# Revit family: Legrand XL³-S 160 flush-mounting
name_source: partatom
category: Equipement électrique
units: mm (PartAtom-declared; Revit-internal decimal feet)

## family parameters
Basée sur le plan de construction = Non
Configuration du panneau = Deux colonnes, circuits au sein
Cote de connecteur circulaire = Utiliser le diamètre
Couper avec des vides une fois chargée = Non
Numéro OmniClass = 23.80.30.11.17
Partagée = Non
Point de calcul de pièce = Non
Titre OmniClass = Distribution Boards and Control Panels
Toujours verticalement = Oui
Type d'élément = Tableau de raccordement

## types (12) — shared parameters
ETIM Class 6.0 = EC000261
Fabricant = Legrand
General Conditions of Use = https://export.legrand.com
IK = 07
IP = 40
Image du type = XL3S160_encastre_337224_p_231245.jpg
Material = Steel
RAL = 9003
URL = www.legrand.fr
depth = 138 mm  [stored 0.452756 ft]
depth Fluxh-mounting = 116 mm  [stored 0.380577 ft]
distance side installation zone = 138 mm  [stored 0.452756 ft]
door = Oui
weight = 0.00 kg
zero-valued in all types: Elévation par défaut

## per-type parameters (varying)
- Distribution envelope - XL³ S 160 Métal - flush-mounting - 24 modules - 2 rows: Cabinet 337222=Oui; Cabinet 337223=Non; Cabinet 337224=Non; Cabinet 337225=Non; Cabinet 337226=Non; Cabinet 337227=Non; Cabinet 337228=Non; Cabinet 337234=Non; Cabinet 337235=Non; Cabinet 337236=Non; Cabinet 337237=Non; Cabinet 337238=Non; Description=337222  Distribution envelope - XL³ S 160 Métal - flush-mounting - 24 modules - 2 rows; depth installation zone=805 mm  [stored 2.64108 ft]; distance before installation zone=667 mm  [stored 2.18832 ft]; door 337252=Oui; door 337253=Non; door 337254=Non; door 337255=Non; door 337256=Non; door 337257=Non; door 337258=Non; door 337264=Non; door 337265=Non; door 337266=Non; door 337267=Non; door 337268=Non; height 1=512 mm  [stored 1.67979 ft]; height 2=440 mm  [stored 1.44357 ft]; module (24 or 36)=24; number row=2; width=667 mm  [stored 2.18832 ft]; width installation zone=943 mm  [stored 3.09383 ft]
- Distribution envelope - XL³ S 160 Métal - flush-mounting - 24 modules - 3 rows: Cabinet 337222=Non; Cabinet 337223=Oui; Cabinet 337224=Non; Cabinet 337225=Non; Cabinet 337226=Non; Cabinet 337227=Non; Cabinet 337228=Non; Cabinet 337234=Non; Cabinet 337235=Non; Cabinet 337236=Non; Cabinet 337237=Non; Cabinet 337238=Non; Description=337223  Distribution envelope - XL³ S 160 Métal - flush-mounting - 24 modules - 3 rows; depth installation zone=805 mm  [stored 2.64108 ft]; distance before installation zone=667 mm  [stored 2.18832 ft]; door 337252=Non; door 337253=Oui; door 337254=Non; door 337255=Non; door 337256=Non; door 337257=Non; door 337258=Non; door 337264=Non; door 337265=Non; door 337266=Non; door 337267=Non; door 337268=Non; height 1=662 mm  [stored 2.17192 ft]; height 2=590 mm  [stored 1.9357 ft]; module (24 or 36)=24; number row=3; width=667 mm  [stored 2.18832 ft]; width installation zone=943 mm  [stored 3.09383 ft]
- Distribution envelope - XL³ S 160 Métal - flush-mounting - 24 modules - 4 rows: Cabinet 337222=Non; Cabinet 337223=Non; Cabinet 337224=Oui; Cabinet 337225=Non; Cabinet 337226=Non; Cabinet 337227=Non; Cabinet 337228=Non; Cabinet 337234=Non; Cabinet 337235=Non; Cabinet 337236=Non; Cabinet 337237=Non; Cabinet 337238=Non; Description=337224  Distribution envelope - XL³ S 160 Métal - flush-mounting - 24 modules - 4 rows; depth installation zone=805 mm  [stored 2.64108 ft]; distance before installation zone=667 mm  [stored 2.18832 ft]; door 337252=Non; door 337253=Non; door 337254=Oui; door 337255=Non; door 337256=Non; door 337257=Non; door 337258=Non; door 337264=Non; door 337265=Non; door 337266=Non; door 337267=Non; door 337268=Non; height 1=812 mm  [stored 2.66404 ft]; height 2=740 mm  [stored 2.42782 ft]; module (24 or 36)=24; number row=4; width=667 mm  [stored 2.18832 ft]; width installation zone=943 mm  [stored 3.09383 ft]
- Distribution envelope - XL³ S 160 Métal - flush-mounting - 24 modules - 5 rows: Cabinet 337222=Non; Cabinet 337223=Non; Cabinet 337224=Non; Cabinet 337225=Oui; Cabinet 337226=Non; Cabinet 337227=Non; Cabinet 337228=Non; Cabinet 337234=Non; Cabinet 337235=Non; Cabinet 337236=Non; Cabinet 337237=Non; Cabinet 337238=Non; Description=337225  Distribution envelope - XL³ S 160 Métal - flush-mounting - 24 modules - 5 rows; depth installation zone=805 mm  [stored 2.64108 ft]; distance before installation zone=667 mm  [stored 2.18832 ft]; door 337252=Non; door 337253=Non; door 337254=Non; door 337255=Oui; door 337256=Non; door 337257=Non; door 337258=Non; door 337264=Non; door 337265=Non; door 337266=Non; door 337267=Non; door 337268=Non; height 1=962 mm  [stored 3.15617 ft]; height 2=890 mm  [stored 2.91995 ft]; module (24 or 36)=24; number row=5; width=667 mm  [stored 2.18832 ft]; width installation zone=943 mm  [stored 3.09383 ft]
- Distribution envelope - XL³ S 160 Métal - flush-mounting - 24 modules - 6 rows: Cabinet 337222=Non; Cabinet 337223=Non; Cabinet 337224=Non; Cabinet 337225=Non; Cabinet 337226=Oui; Cabinet 337227=Non; Cabinet 337228=Non; Cabinet 337234=Non; Cabinet 337235=Non; Cabinet 337236=Non; Cabinet 337237=Non; Cabinet 337238=Non; Description=337226  Distribution envelope - XL³ S 160 Métal - flush-mounting - 24 modules - 6 rows; depth installation zone=805 mm  [stored 2.64108 ft]; distance before installation zone=667 mm  [stored 2.18832 ft]; door 337252=Non; door 337253=Non; door 337254=Non; door 337255=Non; door 337256=Oui; door 337257=Non; door 337258=Non; door 337264=Non; door 337265=Non; door 337266=Non; door 337267=Non; door 337268=Non; height 1=1112 mm  [stored 3.64829 ft]; height 2=1040 mm  [stored 3.41207 ft]; module (24 or 36)=24; number row=6; width=667 mm  [stored 2.18832 ft]; width installation zone=943 mm  [stored 3.09383 ft]
- Distribution envelope - XL³ S 160 Métal - flush-mounting - 24 modules - 7 rows: Cabinet 337222=Non; Cabinet 337223=Non; Cabinet 337224=Non; Cabinet 337225=Non; Cabinet 337226=Non; Cabinet 337227=Oui; Cabinet 337228=Non; Cabinet 337234=Non; Cabinet 337235=Non; Cabinet 337236=Non; Cabinet 337237=Non; Cabinet 337238=Non; Description=337227  Distribution envelope - XL³ S 160 Métal - flush-mounting - 24 modules - 7 rows; depth installation zone=805 mm  [stored 2.64108 ft]; distance before installation zone=667 mm  [stored 2.18832 ft]; door 337252=Non; door 337253=Non; door 337254=Non; door 337255=Non; door 337256=Non; door 337257=Oui; door 337258=Non; door 337264=Non; door 337265=Non; door 337266=Non; door 337267=Non; door 337268=Non; height 1=1262 mm  [stored 4.14042 ft]; height 2=1190 mm  [stored 3.9042 ft]; module (24 or 36)=24; number row=7; width=667 mm  [stored 2.18832 ft]; width installation zone=943 mm  [stored 3.09383 ft]
- Distribution envelope - XL³ S 160 Métal - flush-mounting - 24 modules - 8 rows: Cabinet 337222=Non; Cabinet 337223=Non; Cabinet 337224=Non; Cabinet 337225=Non; Cabinet 337226=Non; Cabinet 337227=Non; Cabinet 337228=Oui; Cabinet 337234=Non; Cabinet 337235=Non; Cabinet 337236=Non; Cabinet 337237=Non; Cabinet 337238=Non; Description=337228  Distribution envelope - XL³ S 160 Métal - flush-mounting - 24 modules - 8 rows; depth installation zone=805 mm  [stored 2.64108 ft]; distance before installation zone=667 mm  [stored 2.18832 ft]; door 337252=Non; door 337253=Non; door 337254=Non; door 337255=Non; door 337256=Non; door 337257=Non; door 337258=Oui; door 337264=Non; door 337265=Non; door 337266=Non; door 337267=Non; door 337268=Non; height 1=1412 mm  [stored 4.63255 ft]; height 2=1340 mm  [stored 4.39633 ft]; module (24 or 36)=24; number row=8; width=667 mm  [stored 2.18832 ft]; width installation zone=943 mm  [stored 3.09383 ft]
- Distribution envelope - XL³ S 160 Métal - flush-mounting - 36 modules - 4 rows: Cabinet 337222=Non; Cabinet 337223=Non; Cabinet 337224=Non; Cabinet 337225=Non; Cabinet 337226=Non; Cabinet 337227=Non; Cabinet 337228=Non; Cabinet 337234=Oui; Cabinet 337235=Non; Cabinet 337236=Non; Cabinet 337237=Non; Cabinet 337238=Non; Description=337234  Distribution envelope - XL³ S 160 Métal - flush-mounting - 36 modules - 4 rows; depth installation zone=1021 mm  [stored 3.34974 ft]; distance before installation zone=883 mm  [stored 2.89698 ft]; door 337252=Non; door 337253=Non; door 337254=Non; door 337255=Non; door 337256=Non; door 337257=Non; door 337258=Non; door 337264=Oui; door 337265=Non; door 337266=Non; door 337267=Non; door 337268=Non; height 1=812 mm  [stored 2.66404 ft]; height 2=740 mm  [stored 2.42782 ft]; module (24 or 36)=36; number row=4; width=883 mm  [stored 2.89698 ft]; width installation zone=1159 mm
- Distribution envelope - XL³ S 160 Métal - flush-mounting - 36 modules - 5 rows: Cabinet 337222=Non; Cabinet 337223=Non; Cabinet 337224=Non; Cabinet 337225=Non; Cabinet 337226=Non; Cabinet 337227=Non; Cabinet 337228=Non; Cabinet 337234=Non; Cabinet 337235=Oui; Cabinet 337236=Non; Cabinet 337237=Non; Cabinet 337238=Non; Description=337235  Distribution envelope - XL³ S 160 Métal - flush-mounting - 36 modules - 5 rows; depth installation zone=1021 mm  [stored 3.34974 ft]; distance before installation zone=883 mm  [stored 2.89698 ft]; door 337252=Non; door 337253=Non; door 337254=Non; door 337255=Non; door 337256=Non; door 337257=Non; door 337258=Non; door 337264=Non; door 337265=Oui; door 337266=Non; door 337267=Non; door 337268=Non; height 1=962 mm  [stored 3.15617 ft]; height 2=890 mm  [stored 2.91995 ft]; module (24 or 36)=36; number row=5; width=883 mm  [stored 2.89698 ft]; width installation zone=1159 mm
- Distribution envelope - XL³ S 160 Métal - flush-mounting - 36 modules - 6 rows: Cabinet 337222=Non; Cabinet 337223=Non; Cabinet 337224=Non; Cabinet 337225=Non; Cabinet 337226=Non; Cabinet 337227=Non; Cabinet 337228=Non; Cabinet 337234=Non; Cabinet 337235=Non; Cabinet 337236=Oui; Cabinet 337237=Non; Cabinet 337238=Non; Description=337236  Distribution envelope - XL³ S 160 Métal - flush-mounting - 36 modules - 6 rows; depth installation zone=1021 mm  [stored 3.34974 ft]; distance before installation zone=883 mm  [stored 2.89698 ft]; door 337252=Non; door 337253=Non; door 337254=Non; door 337255=Non; door 337256=Non; door 337257=Non; door 337258=Non; door 337264=Non; door 337265=Non; door 337266=Oui; door 337267=Non; door 337268=Non; height 1=1112 mm  [stored 3.64829 ft]; height 2=1040 mm  [stored 3.41207 ft]; module (24 or 36)=36; number row=6; width=883 mm  [stored 2.89698 ft]; width installation zone=1159 mm
- Distribution envelope - XL³ S 160 Métal - flush-mounting - 36 modules - 7 rows: Cabinet 337222=Non; Cabinet 337223=Non; Cabinet 337224=Non; Cabinet 337225=Non; Cabinet 337226=Non; Cabinet 337227=Non; Cabinet 337228=Non; Cabinet 337234=Non; Cabinet 337235=Non; Cabinet 337236=Non; Cabinet 337237=Oui; Cabinet 337238=Non; Description=337237  Distribution envelope - XL³ S 160 Métal - flush-mounting - 36 modules - 7 rows; depth installation zone=1021 mm  [stored 3.34974 ft]; distance before installation zone=883 mm  [stored 2.89698 ft]; door 337252=Non; door 337253=Non; door 337254=Non; door 337255=Non; door 337256=Non; door 337257=Non; door 337258=Non; door 337264=Non; door 337265=Non; door 337266=Non; door 337267=Oui; door 337268=Non; height 1=1262 mm  [stored 4.14042 ft]; height 2=1190 mm  [stored 3.9042 ft]; module (24 or 36)=36; number row=7; width=883 mm  [stored 2.89698 ft]; width installation zone=1159 mm
- Distribution envelope - XL³ S 160 Métal - flush-mounting - 36 modules - 8 rows: Cabinet 337222=Non; Cabinet 337223=Non; Cabinet 337224=Non; Cabinet 337225=Non; Cabinet 337226=Non; Cabinet 337227=Non; Cabinet 337228=Non; Cabinet 337234=Non; Cabinet 337235=Non; Cabinet 337236=Non; Cabinet 337237=Non; Cabinet 337238=Oui; Description=337238  Distribution envelope - XL³ S 160 Métal - flush-mounting - 36 modules - 8 rows; depth installation zone=1021 mm  [stored 3.34974 ft]; distance before installation zone=883 mm  [stored 2.89698 ft]; door 337252=Non; door 337253=Non; door 337254=Non; door 337255=Non; door 337256=Non; door 337257=Non; door 337258=Non; door 337264=Non; door 337265=Non; door 337266=Non; door 337267=Non; door 337268=Oui; height 1=1412 mm  [stored 4.63255 ft]; height 2=1340 mm  [stored 4.39633 ft]; module (24 or 36)=36; number row=8; width=883 mm  [stored 2.89698 ft]; width installation zone=1159 mm

note: [stored X ft] marks values corroborated as IEEE doubles in the binary element streams (Revit-internal decimal feet)
